# Revit family: Hager-WITTY PRO WALL MOUNTED-it-CH-CH
name_source: partatom
category: Electrical Fixtures
units: mm (PartAtom-declared; Revit-internal decimal feet)

## family parameters
Always vertical = Yes
Cut with Voids When Loaded = No
Host = Wall
Maintain Annotation Orientation = No
OmniClass Number = 23.75.00.00
OmniClass Title = Climate Control (HVAC)
Part Type = Normal
Room Calculation Point = No
Round Connector Dimension = Use Diameter
Shared = No

## types (2) — shared parameters
BC_METADATA = {"ObjectGuid":"b7395028-ef9e-46b8-b49f-e0fe9c8fa070","ModelGuid":"b1efb829-c177-4a88-8b0d-f632edc25d22","VariantGuid":"c7b0c534-fef0-4725-a2d6-e8a658ebdb92","Revision":"#2","VariantName":"REF 1"}
BC_MODEL_ID = 1528885
BC_OBJECT_ID = 511149
BC_OBJECT_VERSION = #1
Code hager = ADD_EC002883_ECVS_WO
EF000003 - modo di montaggio = montaggio a parete
EF000008 - larghezza = 250 mm  [stored 0.82021 ft]
EF000040 - altezza = 370 mm  [stored 1.21391 ft]
EF000049 - profondità = 150 mm  [stored 0.492126 ft]
EF000458 - con display = No
EF001596 - materiale della scatola = materiale sintetico
EF002136 - potenza allacciata nominale = 22000 W
EF003840 - tensione d'ingresso = 400 V
EF004293 - resistenza agli urti = IK10
EF005455 - frequenza = 50/60 Hz
EF005474 - grado di protezione (IP) = IP55
EF007001 - tensione d'uscita DC = 0 V
EF007353 - corrente d'uscita max. DC = 0 A
EF009078 - numero dei punti di carica = 1
EF009089 - coffano d'abbonati = No
EF009300 - potenza massima per punto di carica = 22000 W
EF009305 - numero di prese di carica tipo 2 = 1
EF009313 - con contatore d'energia = Yes
EF009314 - con disguintore = No
EF009547 - LTE = No
EF011072 - compatibile IFTTT = No
EF012191 - con lettore scheda RFID integrato = Yes
EF012361 - NFC (Near Field Communication) = No
EF013154 - collegabile via Wi-Fi = Yes
EF014925 - compatibile con Apple HomeKit = No
EF014926 - compatibile con Google Assistant = No
EF014927 - compatibile con Amazon Alexa = No
EF016385 - standard di telefonia mobile 5G = No
EF017508 - può essere collegato in rete come master = No
EF017509 - rilevamento della corrente di guasto DC = No
EF017510 - rilevamento delle saldature dei contattori = No
EF017511 - con interruttore a chiave = No
EF017512 - esportazione della cronologia dei carichi = Yes
EF017513 - Open Charge Point Protocol (OCPP) versione = 1.6
EF017515 - Plug and charge (ISO 15118) = No
EF017517 - può essere collegato in rete come estensione = No
EF017663 - cavo di ricarica bloccabile costantemente sulla stazione di ricarica = No
EF017664 - può essere collegato in rete tramite LAN = Yes
EF017665 - con contatore di energia compatibile MID = Yes
EF017668 - gestione integrata del carico statico = No
EF017669 - adatto per la gestione dinamica del carico = Yes
EF017672 - backend integrato = No
EF017972 - utilizzo e configurazione tramite app = Yes
EF025053 - tipo di collegamento lato impianto = trifase
EFDE0066 - conforme alla legislazione sulla calibrazione = No
ETIM class code = EC002883
ETIM class name = Charging device E-Mobility
HG000003-Range = WITTY PRO
HG000065-With socket TE = No
HG000099-Onfly Template ID = WittyOne_EVCS_Wall_Mounted
Manufacturer = hager France
Name = WITTY PRO WALL MOUNTED-CH
Name BIM&CO = Electricity
Name hager = ADD_ChargingStation_EC002883
Reference description = ECVS Witty 1x22kW 3P T2S
zero-valued in all types: Default Elevation, EF006577 - numero di prese CEE (IEC 60309), EF008200 - sezione conduttore collegabile, EF009091 - numero di disgiuntori differenziali tipo A, EF009092 - numero di disgiuntori differenziali tipo B, EF009301 - numero di connettori di carica tipo 1, EF009302 - numero di connettori di carica tipo 1 CCS, EF009303 - numero di connettori di carica tipo 2, EF009304 - numero di connettori di carica tipo 2 CCS, EF009306 - numero di connettori di carica GB AC, EF009307 - numero di connettori di carica GB DC, EF009308 - numero di prese di carica GB, EF009309 - numero di prese di carica tipo 3, EF009310 - numero di connettori di carica CHAdeMO, EF009311 - numero di prese domestiche

## per-type parameters (varying)
| type | BC_VARIANT_ID | EF014895 - lunghezza del cavo di carico | HG000004-Manufacturer reference |
| WITTY PRO-1x22kW-3P-XVL122SCH-WALL MOUNTED | 1164666 | 0 mm  [stored 0 ft] | XVL122SCH |
| WITTY PRO-1x22kW-3P-XVL122CCH-WALL MOUNTED | 1164667 | 6500 mm  [stored 21.3255 ft] | XVL122CCH |

note: column(s) folded — value = type name in every type: Reference

note: [stored X ft] marks values corroborated as IEEE doubles in the binary element streams (Revit-internal decimal feet)
